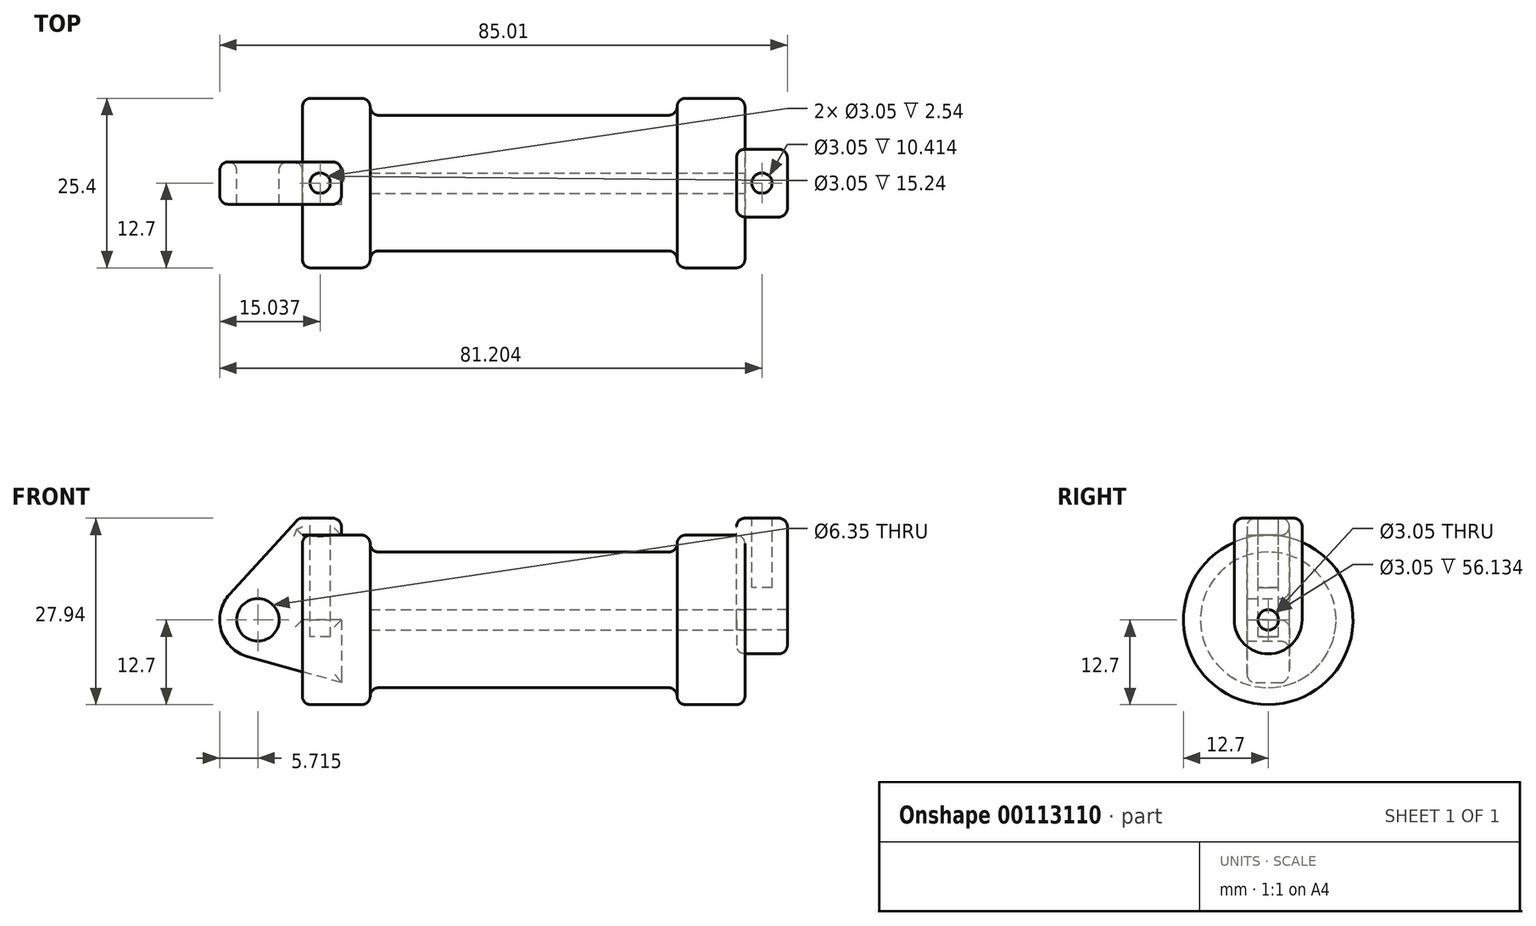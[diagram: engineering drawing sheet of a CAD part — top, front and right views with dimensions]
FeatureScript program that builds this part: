
annotation { "Feature Type Name" : "Feature", "Feature Type Description" : "" }
export const myFeature = defineFeature(function(context is Context, id is Id, definition is map)
    precondition{}
    {
        {
            var Q0;
            Q0=qCreatedBy(makeId("Front.planeOp"),FACE);
            var sketch = newSketch(context, id + "F0", { "sketchPlane" : qUnion([Q0])});
            skLineSegment(sketch, "E0", {"start": v(0, 0) * mm, "end": v(0, 12.7) * mm});
            skLineSegment(sketch, "E1", {"start": v(0, 12.7) * mm, "end": v(10.16, 12.7) * mm});
            skLineSegment(sketch, "E2", {"start": v(10.16, 12.7) * mm, "end": v(10.16, 10.16) * mm});
            skLineSegment(sketch, "E3", {"start": v(10.16, 10.16) * mm, "end": v(56.13, 10.16) * mm});
            skLineSegment(sketch, "E4", {"start": v(56.13, 10.16) * mm, "end": v(56.13, 12.7) * mm});
            skLineSegment(sketch, "E5", {"start": v(56.13, 12.7) * mm, "end": v(66.3, 12.7) * mm});
            skLineSegment(sketch, "E6", {"start": v(66.3, 12.7) * mm, "end": v(66.3, 0) * mm});
            skLineSegment(sketch, "E7", {"start": v(66.3, 0) * mm, "end": v(0, 0) * mm});
            skLineSegment(sketch, "E8", {"start": v(5.84, 15.24) * mm, "end": v(-0.5, 15.24) * mm});
            skLineSegment(sketch, "E9", {"start": v(-0.5, 15.24) * mm, "end": v(-10.88, 3.85) * mm});
            skLineSegment(sketch, "E10", {"start": v(0, 0) * mm, "end": v(-6.65, 0) * mm});
            skCircle(sketch, "E11", {"center": v(-6.65, 0) * mm, "radius": 5.72 * mm});
            skCircle(sketch, "E12", {"center": v(-6.65, 0) * mm, "radius": 3.18 * mm});
            skLineSegment(sketch, "E13", {"start": v(5.84, 15.24) * mm, "end": v(5.84, -9.4) * mm});
            skLineSegment(sketch, "E14", {"start": v(5.84, -9.4) * mm, "end": v(-8.18, -5.5) * mm});
            skSolve(sketch);
        }
        {
            var Q0;
            {var subQ0=sQuery(id+"F0.wireOp",EDGE,"E2");Q0=makeQuery(id+"F0.imprint","IMPRINT",FACE,{"disambiguationData":[TD([[makeQuery(id+"F0.imprint","IMPRINT",EDGE,{"derivedFrom":subQ0}),-1.0]])]});}
            var Q1;
            {var subQ0=sQuery(id+"F0.wireOp",EDGE,"E0");Q1=makeQuery(id+"F0.imprint","IMPRINT",FACE,{"disambiguationData":[TD([[makeQuery(id+"F0.imprint","IMPRINT",EDGE,{"derivedFrom":subQ0}),-1.0]])]});}
            var Q2;
            Q2=sQuery(id+"F0.wireOp",EDGE,"E7");
            revolve(context, id + "F1", {"entities" : qUnion([Q0, Q1]), "axis" : qUnion([Q2]), "revolveType" : RevolveType.FULL});
        }
        {
            var Q0;
            {var subQ3=sQuery(id+"F0.wireOp",EDGE,"E0");Q0=makeQuery(id+"F0.imprint","IMPRINT",FACE,{"disambiguationData":[TD([[makeQuery(id+"F0.imprint","IMPRINT",EDGE,{"derivedFrom":subQ3}),1.0]])]});}
            var Q1;
            {var subQ4=sQuery(id+"F0.wireOp",EDGE,"E12");Q1=makeQuery(id+"F0.imprint","IMPRINT",FACE,{"disambiguationData":[TD([[makeQuery(id+"F0.imprint","IMPRINT",EDGE,{"derivedFrom":subQ4}),-1.0]])]});}
            var Q2;
            {var subQ0=sQuery(id+"F0.wireOp",EDGE,"E14");Q2=makeQuery(id+"F0.imprint","IMPRINT",FACE,{"disambiguationData":[TD([[makeQuery(id+"F0.imprint","IMPRINT",EDGE,{"derivedFrom":subQ0}),-1.0]])]});}
            extrude(context, id + "F2", {"entities" : qUnion([Q0, Q1, Q2]), "endBound" : BoundingType.SYMMETRIC, "depth" : 6.35 * mm});
        }
        {
            var Q0;
            Q0=makeQuery(id+"F1.opRevolve","SWEPT_FACE",FACE,{"disambiguationData":[OSD([sQuery(id+"F0.wireOp",EDGE,"E6")])]});
            var sketch = newSketch(context, id + "F3", { "sketchPlane" : qUnion([Q0])});
            skCircle(sketch, "E15", {"center": v(0, 0) * mm, "radius": 1.52 * mm});
            skCircle(sketch, "E16", {"center": v(0, 0) * mm, "radius": 5.08 * mm});
            skLineSegment(sketch, "E17", {"start": v(5.08, 0) * mm, "end": v(5.08, 15.24) * mm});
            skLineSegment(sketch, "E18", {"start": v(-5.08, 0) * mm, "end": v(-5.08, 15.24) * mm});
            skLineSegment(sketch, "E19", {"start": v(-5.08, 15.24) * mm, "end": v(5.08, 15.24) * mm});
            skSolve(sketch);
        }
        {
            var Q0;
            {var subQ0=sQuery(id+"F3.wireOp",EDGE,"E19");Q0=makeQuery(id+"F3.imprint","IMPRINT",FACE,{"disambiguationData":[TD([[makeQuery(id+"F3.imprint","IMPRINT",EDGE,{"derivedFrom":subQ0}),-1.0]])]});}
            var Q1;
            {var subQ0=sQuery(id+"F3.wireOp",EDGE,"E17");var subQ1=sQuery(id+"F3.wireOp",EDGE,"E16");var subQ2=makeQuery(id+"F3.imprint","INTERSECT",VERTEX,{"derivedFrom":[subQ1,subQ0]});Q1=makeQuery(id+"F3.imprint","IMPRINT",FACE,{"disambiguationData":[TD([[makeQuery(id+"F3.imprint","IMPRINT",EDGE,{"disambiguationData":[TD([[subQ2,-1.0]])],"derivedFrom":subQ1}),-1.0]])]});}
            var Q2;
            Q2=makeQuery(id+"F3.imprint","IMPRINT",FACE,{"disambiguationData":[TD([[makeQuery(id+"F3.imprint","IMPRINT",EDGE,{"derivedFrom":sQuery(id+"F3.wireOp",EDGE,"E15")}),-1.0]])]});
            extrude(context, id + "F4", {"entities" : qUnion([Q0, Q1, Q2]), "depth" : 6.35 * mm, "hasSecondDirection" : true, "secondDirectionOppositeDirection" : true, "secondDirectionDepth" : 1.27 * mm});
        }
        {
            var Q0;
            Q0=makeQuery(id+"F1.opRevolve","SWEPT_FACE",FACE,{"disambiguationData":[OSD([sQuery(id+"F0.wireOp",EDGE,"E6")])]});
            var sketch = newSketch(context, id + "F5", { "sketchPlane" : qUnion([Q0])});
            skCircle(sketch, "E20", {"center": v(0, 0) * mm, "radius": 1.52 * mm});
            skSolve(sketch);
        }
        {
            var Q0;
            Q0=makeQuery(id+"F5.imprint","IMPRINT",FACE,{"disambiguationData":[TD([[makeQuery(id+"F5.imprint","IMPRINT",EDGE,{"derivedFrom":sQuery(id+"F5.wireOp",EDGE,"E20")}),1.0]])]});
            var Q1;
            Q1=makeQuery(id+"F1.opRevolve","SWEPT_FACE",FACE,{"disambiguationData":[OSD([sQuery(id+"F0.wireOp",EDGE,"E2")])]});
            extrude(context, id + "F6", {"entities" : qUnion([Q0]), "operationType" : NewBodyOperationType.REMOVE, "endBound" : BoundingType.UP_TO_SURFACE, "oppositeDirection" : true, "endBoundEntityFace" : qUnion([Q1]), "depth" : 25.4 * mm});
        }
        {
            var Q0;
            Q0=makeQuery(id+"F4.opExtrude","SWEPT_FACE",FACE,{"disambiguationData":[OSD([sQuery(id+"F3.wireOp",EDGE,"E19")])]});
            var sketch = newSketch(context, id + "F7", { "sketchPlane" : qUnion([Q0])});
            skCircle(sketch, "E21", {"center": v(68.83, 0) * mm, "radius": 1.52 * mm});
            skPoint(sketch, "E21.centerSnap0", {"position": v(65.02, 0) * mm});
            skPoint(sketch, "E21.centerSnap1", {"position": v(68.83, -5.08) * mm});
            skSolve(sketch);
        }
        {
            var Q0;
            Q0=makeQuery(id+"F7.imprint","IMPRINT",FACE,{"disambiguationData":[TD([[makeQuery(id+"F7.imprint","IMPRINT",EDGE,{"derivedFrom":sQuery(id+"F7.wireOp",EDGE,"E21")}),1.0]])]});
            var Q1;
            Q1=sQuery(id+"F7.wireOp",EDGE,"E21");
            extrude(context, id + "F8", {"entities" : qUnion([Q0]), "operationType" : NewBodyOperationType.REMOVE, "surfaceEntities" : qUnion([Q1]), "oppositeDirection" : true, "depth" : 10.4 * mm});
        }
        {
            var Q0;
            Q0=makeQuery(id+"F2.opExtrude","SWEPT_FACE",FACE,{"disambiguationData":[OSD([sQuery(id+"F0.wireOp",EDGE,"E8")])]});
            var sketch = newSketch(context, id + "F9", { "sketchPlane" : qUnion([Q0])});
            skCircle(sketch, "E22", {"center": v(2.67, 0) * mm, "radius": 1.52 * mm});
            skPoint(sketch, "E22.centerSnap0", {"position": v(-0.5, 0) * mm});
            skSolve(sketch);
        }
        {
            var Q0;
            Q0=makeQuery(id+"F9.imprint","IMPRINT",FACE,{"disambiguationData":[TD([[makeQuery(id+"F9.imprint","IMPRINT",EDGE,{"derivedFrom":sQuery(id+"F9.wireOp",EDGE,"E22")}),1.0]])]});
            extrude(context, id + "F10", {"entities" : qUnion([Q0]), "operationType" : NewBodyOperationType.REMOVE, "oppositeDirection" : true, "depth" : 17.78 * mm});
        }
        {
            var Q0;
            Q0=makeQuery(id+"F1.opRevolve","SWEPT_FACE",FACE,{"disambiguationData":[OSD([sQuery(id+"F0.wireOp",EDGE,"E3")])]});
            var Q1;
            Q1=makeQuery(id+"F1.opRevolve","SWEPT_EDGE",EDGE,{"disambiguationData":[OSD([sQuery(id+"F0.wireOp",EDGE,"E4"),sQuery(id+"F0.wireOp",EDGE,"E5")])]});
            var Q2;
            Q2=makeQuery(id+"F1.opRevolve","SWEPT_EDGE",EDGE,{"disambiguationData":[OSD([sQuery(id+"F0.wireOp",EDGE,"E1"),sQuery(id+"F0.wireOp",EDGE,"E2")])]});
            var Q3;
            Q3=makeQuery(id+"F1.opRevolve","SWEPT_EDGE",EDGE,{"disambiguationData":[OSD([sQuery(id+"F0.wireOp",EDGE,"E5"),sQuery(id+"F0.wireOp",EDGE,"E6")])]});
            var Q4;
            Q4=makeQuery(id+"F1.opRevolve","SWEPT_EDGE",EDGE,{"disambiguationData":[OSD([sQuery(id+"F0.wireOp",EDGE,"E0"),sQuery(id+"F0.wireOp",EDGE,"E1")])]});
            var Q5;
            Q5=makeQuery(id+"F4.opExtrude","CAP_EDGE",EDGE,{"disambiguationData":[OSD([sQuery(id+"F3.wireOp",EDGE,"E17")])],"isStart":false});
            var Q6;
            Q6=makeQuery(id+"F4.opExtrude","SWEPT_EDGE",EDGE,{"disambiguationData":[OSD([sQuery(id+"F3.wireOp",EDGE,"E17"),sQuery(id+"F3.wireOp",EDGE,"E19")])]});
            var Q7;
            Q7=makeQuery(id+"F4.opExtrude","CAP_EDGE",EDGE,{"disambiguationData":[OSD([sQuery(id+"F3.wireOp",EDGE,"E17")])],"isStart":true});
            var Q8;
            Q8=makeQuery(id+"F4.opExtrude","SWEPT_EDGE",EDGE,{"disambiguationData":[OSD([sQuery(id+"F3.wireOp",EDGE,"E18"),sQuery(id+"F3.wireOp",EDGE,"E19")])]});
            var Q9;
            Q9=makeQuery(id+"F4.opExtrude","CAP_EDGE",EDGE,{"disambiguationData":[OSD([sQuery(id+"F3.wireOp",EDGE,"E19")])],"isStart":true});
            var Q10;
            Q10=makeQuery(id+"F2.opExtrude","CAP_EDGE",EDGE,{"disambiguationData":[OSD([sQuery(id+"F0.wireOp",EDGE,"E11")])],"isStart":false});
            var Q11;
            Q11=makeQuery(id+"F2.opExtrude","CAP_FACE",FACE,{"disambiguationData":[OSD([sQuery(id+"F0.wireOp",EDGE,"E0"),sQuery(id+"F0.wireOp",EDGE,"E1"),sQuery(id+"F0.wireOp",EDGE,"E7"),sQuery(id+"F0.wireOp",EDGE,"E8"),sQuery(id+"F0.wireOp",EDGE,"E9"),sQuery(id+"F0.wireOp",EDGE,"E11"),sQuery(id+"F0.wireOp",EDGE,"E12"),sQuery(id+"F0.wireOp",EDGE,"E13"),sQuery(id+"F0.wireOp",EDGE,"E14")])],"isStart":true});
            var Q12;
            Q12=makeQuery(id+"F2.opExtrude","SWEPT_EDGE",EDGE,{"disambiguationData":[OSD([sQuery(id+"F0.wireOp",EDGE,"E8"),sQuery(id+"F0.wireOp",EDGE,"E13")])]});
            var Q13;
            {var subQ0=sQuery(id+"F0.wireOp",EDGE,"E13");Q13=makeQuery(id+"F2.opExtrude","CAP_EDGE",EDGE,{"disambiguationData":[OSD([subQ0]),TDD([makeQuery(id+"F0.imprint","IMPRINT",EDGE,{"disambiguationData":[TD([[makeQuery(id+"F0.imprint","INTERSECT",VERTEX,{"derivedFrom":[sQuery(id+"F0.wireOp",EDGE,"E8"),subQ0]}),-1.0]])],"derivedFrom":subQ0})])],"isStart":false});}
            var Q14;
            Q14=makeQuery(id+"F2.opExtrude","SWEPT_EDGE",EDGE,{"disambiguationData":[OSD([sQuery(id+"F0.wireOp",EDGE,"E8"),sQuery(id+"F0.wireOp",EDGE,"E9")])]});
            var Q15;
            Q15=makeQuery(id+"F2.opExtrude","CAP_EDGE",EDGE,{"disambiguationData":[OSD([sQuery(id+"F0.wireOp",EDGE,"E8")])],"isStart":false});
            var Q16;
            Q16=makeQuery(id+"F4.opExtrude","CAP_EDGE",EDGE,{"disambiguationData":[OSD([sQuery(id+"F3.wireOp",EDGE,"E19")])],"isStart":false});
            fillet(context, id + "F11", {"entities" : qUnion([Q0, Q1, Q2, Q3, Q4, Q5, Q6, Q7, Q8, Q9, Q10, Q11, Q12, Q13, Q14, Q15, Q16]), "radius" : 1.27 * mm, "tangentPropagation" : true, "allowEdgeOverflow" : false});
        }
    });
